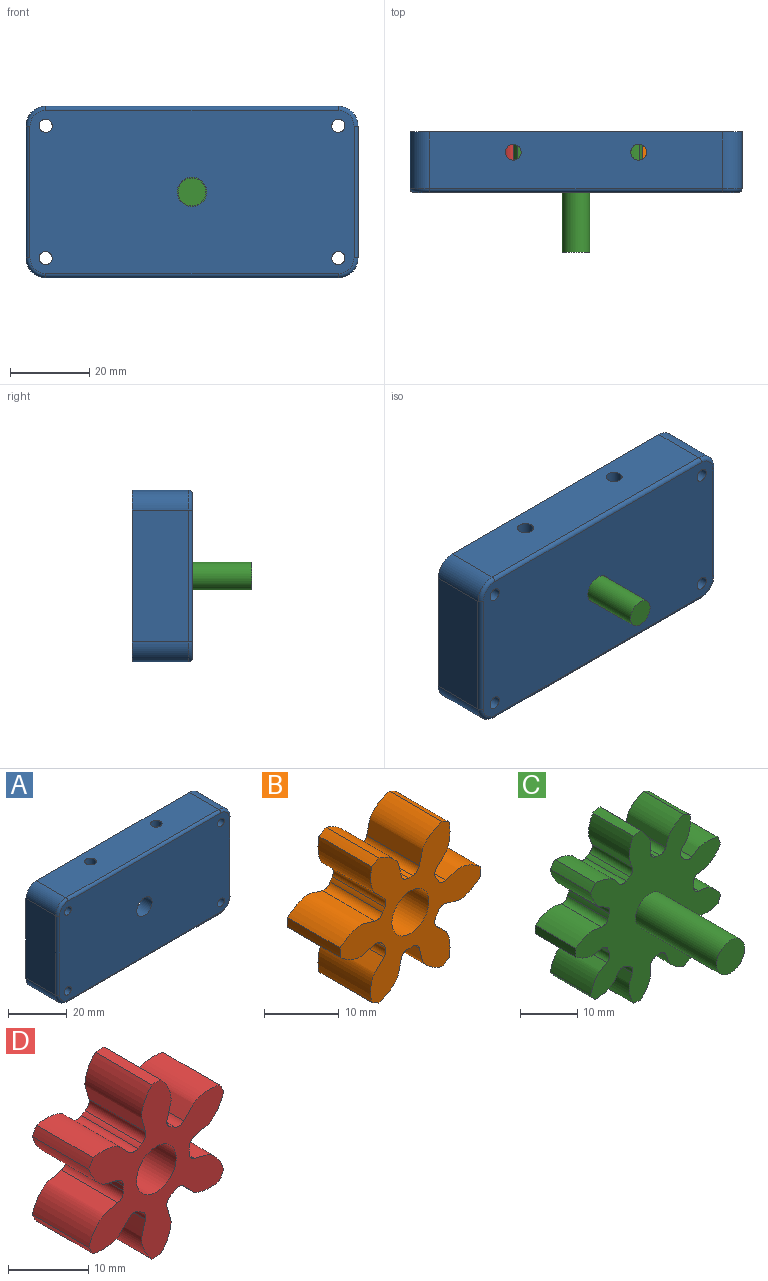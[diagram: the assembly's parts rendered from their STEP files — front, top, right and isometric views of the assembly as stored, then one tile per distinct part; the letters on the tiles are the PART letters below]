
ASSEMBLY  parts=4 mates=3
PART A: 36 faces, bbox 84.4x15.2x44 mm
  f0: cylinder r=13.6mm len=27.2mm, axis (0,1,0), area 631.5mm2, adj f1,f7,f8,f9,f12,f14
  f1: cylinder r=18.6mm len=31.59mm, axis (0,1,0), area 363.6mm2, adj f0,f2,f8,f9,f14,f15
  f2: cylinder r=13.6mm len=27.2mm, axis (0,1,0), area 631.5mm2, adj f1,f7,f8,f9,f13,f15
  f3: plane 33.2x14.2mm, normal (1,0,0), area 471.4mm2, adj f8,f20,f23,f27
  f4: plane 73.6x14.2mm, normal (0,0,1), area 1020mm2, adj f8,f14,f15,f20,f21,f24
  f5: plane 33.2x14.2mm, normal (-1,0,0), area 471.4mm2, adj f8,f21,f22,f28
  f6: plane 73.6x14.2mm, normal (0,0,-1), area 1020mm2, adj f8,f12,f13,f22,f23,f31
  f7: cylinder r=18.6mm len=31.59mm, axis (0,1,0), area 363.6mm2, adj f0,f2,f8,f9,f12,f13
  f8: plane 83.6x43.2mm, normal (0,1,0), area 1495.3mm2, adj f0,f1,f2,f3,f4,f5,f6,f7
  f9: plane 77.6x37.2mm, normal (0,1,0), area 1949.1mm2, adj f0,f1,f2,f7,f11,f32,f34
  f10: plane 81.6x41.2mm, normal (0,-1,0), area 3271mm2, adj f11,f16,f17,f18,f19,f24,f25,f26
  f11: cylinder r=3.7mm len=7.4mm, axis (0,-1,0), area 116.2mm2, adj f9,f10
  f12: cylinder r=2mm len=11.78mm, axis (0,0,1), area 130.4mm2, adj f0,f6,f7
  f13: cylinder r=2mm len=11.78mm, axis (0,0,1), area 130.4mm2, adj f2,f6,f7
  f14: cylinder r=2mm len=11.78mm, axis (0,0,1), area 130.4mm2, adj f0,f1,f4
  f15: cylinder r=2mm len=11.78mm, axis (0,0,1), area 130.4mm2, adj f1,f2,f4
  f16: cylinder r=1.65mm len=15.2mm, axis (0,1,0), area 157.6mm2, adj f8,f10
  f17: cylinder r=1.65mm len=15.2mm, axis (0,1,0), area 157.6mm2, adj f8,f10
  f18: cylinder r=1.65mm len=15.2mm, axis (0,1,0), area 157.6mm2, adj f8,f10
  f19: cylinder r=1.65mm len=15.2mm, axis (0,1,0), area 157.6mm2, adj f8,f10
  f20: cylinder r=5mm len=14.2mm, axis (0,-1,0), area 111.5mm2, adj f3,f4,f8,f25
  f21: cylinder r=5mm len=14.2mm, axis (0,1,0), area 111.5mm2, adj f4,f5,f8,f26
  f22: cylinder r=5mm len=14.2mm, axis (0,-1,0), area 111.5mm2, adj f5,f6,f8,f30
  f23: cylinder r=5mm len=14.2mm, axis (0,1,0), area 111.5mm2, adj f3,f6,f8,f29
  f24: cylinder r=1mm len=73.6mm, axis (1,0,0), area 115.6mm2, adj f4,f10,f25,f26
  f25: torus R=4mm, axis (0,-1,0), area 11.4mm2, adj f10,f20,f24,f27
  f26: torus R=4mm, axis (0,-1,0), area 11.4mm2, adj f10,f21,f24,f28
  f27: cylinder r=1mm len=33.2mm, axis (0,0,-1), area 52.2mm2, adj f3,f10,f25,f29
  f28: cylinder r=1mm len=33.2mm, axis (0,0,1), area 52.2mm2, adj f5,f10,f26,f30
  f29: torus R=4mm, axis (0,-1,0), area 11.4mm2, adj f10,f23,f27,f31
  f30: torus R=4mm, axis (0,-1,0), area 11.4mm2, adj f10,f22,f28,f31
  f31: cylinder r=1mm len=73.6mm, axis (-1,0,0), area 115.6mm2, adj f6,f10,f29,f30
  f32: cylinder r=3.3mm len=10.2mm, axis (0,-1,0), area 211.5mm2, adj f9,f33
  f33: plane 6.6x6.6mm, normal (0,1,0), area 34.2mm2, adj f32
  f34: cylinder r=3.3mm len=10.2mm, axis (0,-1,0), area 211.5mm2, adj f9,f35
  f35: plane 6.6x6.6mm, normal (0,1,0), area 34.2mm2, adj f34
PART B: 39 faces, bbox 26.8x10x24 mm
  f0: cylinder r=13.33mm len=10mm, axis (0,1,0), area 15.7mm2, adj f5,f7,f23,f35
  f1: cylinder r=13.33mm len=10mm, axis (0,1,0), area 15.7mm2, adj f5,f7,f30,f33
  f2: cylinder r=13.33mm len=10mm, axis (0,1,0), area 15.7mm2, adj f5,f7,f18,f25
  f3: cylinder r=13.33mm len=10mm, axis (0,1,0), area 15.7mm2, adj f5,f7,f8,f20
  f4: cylinder r=13.33mm len=10mm, axis (0,1,0), area 15.7mm2, adj f5,f7,f15,f28
  f5: plane 26.81x24.03mm, normal (0,-1,0), area 257.9mm2, adj f0,f1,f2,f3,f4,f6,f8,f9
  f6: cylinder r=13.33mm len=10mm, axis (0,1,0), area 15.7mm2, adj f5,f7,f10,f13
  f7: plane 26.81x24.03mm, normal (0,1,0), area 257.9mm2, adj f0,f1,f2,f3,f4,f6,f8,f9
  f8: extruded ~10x6.28mm, area 71.4mm2, adj f3,f5,f7,f11
  f9: cylinder r=5.83mm len=10mm, axis (0,1,0), area 8mm2, adj f5,f7,f11,f12
  f10: extruded ~10x6.6mm, area 71.4mm2, adj f5,f6,f7,f12
  f11: cylinder r=1.26mm len=10mm, axis (0,1,0), area 17.5mm2, adj f5,f7,f8,f9
  f12: cylinder r=1.26mm len=10mm, axis (0,1,0), area 17.5mm2, adj f5,f7,f9,f10
  f13: extruded ~10x6.6mm, area 71.4mm2, adj f5,f6,f7,f16
  f14: cylinder r=5.83mm len=10mm, axis (0,1,0), area 8mm2, adj f5,f7,f16,f17
  f15: extruded ~10x6.28mm, area 71.4mm2, adj f4,f5,f7,f17
  f16: cylinder r=1.26mm len=10mm, axis (0,1,0), area 17.5mm2, adj f5,f7,f13,f14
  f17: cylinder r=1.26mm len=10mm, axis (0,1,0), area 17.5mm2, adj f5,f7,f14,f15
  f18: extruded ~10x5.15mm, area 71.4mm2, adj f2,f5,f7,f21
  f19: cylinder r=5.83mm len=10mm, axis (0,1,0), area 8mm2, adj f5,f7,f21,f22
  f20: extruded ~10x5.15mm, area 71.4mm2, adj f3,f5,f7,f22
  f21: cylinder r=1.26mm len=10mm, axis (0,1,0), area 17.5mm2, adj f5,f7,f18,f19
  f22: cylinder r=1.26mm len=10mm, axis (0,1,0), area 17.5mm2, adj f5,f7,f19,f20
  f23: extruded ~10x6.6mm, area 71.4mm2, adj f0,f5,f7,f26
  f24: cylinder r=5.83mm len=10mm, axis (0,1,0), area 8mm2, adj f5,f7,f26,f27
  f25: extruded ~10x6.28mm, area 71.4mm2, adj f2,f5,f7,f27
  f26: cylinder r=1.26mm len=10mm, axis (0,1,0), area 17.5mm2, adj f5,f7,f23,f24
  f27: cylinder r=1.26mm len=10mm, axis (0,1,0), area 17.5mm2, adj f5,f7,f24,f25
  f28: extruded ~10x5.15mm, area 71.4mm2, adj f4,f5,f7,f31
  f29: cylinder r=5.83mm len=10mm, axis (0,1,0), area 8mm2, adj f5,f7,f31,f32
  f30: extruded ~10x5.15mm, area 71.4mm2, adj f1,f5,f7,f32
  f31: cylinder r=1.26mm len=10mm, axis (0,1,0), area 17.5mm2, adj f5,f7,f28,f29
  f32: cylinder r=1.26mm len=10mm, axis (0,1,0), area 17.5mm2, adj f5,f7,f29,f30
  f33: extruded ~10x6.28mm, area 71.4mm2, adj f1,f5,f7,f36
  f34: cylinder r=5.83mm len=10mm, axis (0,1,0), area 8mm2, adj f5,f7,f36,f37
  f35: extruded ~10x6.6mm, area 71.4mm2, adj f0,f5,f7,f37
  f36: cylinder r=1.26mm len=10mm, axis (0,1,0), area 17.5mm2, adj f5,f7,f33,f34
  f37: cylinder r=1.26mm len=10mm, axis (0,1,0), area 17.5mm2, adj f5,f7,f34,f35
  f38: cylinder r=3.5mm len=10mm, axis (0,-1,0), area 219.9mm2, adj f5,f7
PART C: 58 faces, bbox 36x30x36.5 mm
  f0: cylinder r=18.33mm len=10mm, axis (0,1,0), area 18.9mm2, adj f8,f10,f36,f53
  f1: cylinder r=18.33mm len=10mm, axis (0,1,0), area 18.9mm2, adj f8,f10,f48,f51
  f2: cylinder r=18.33mm len=10mm, axis (0,1,0), area 18.9mm2, adj f8,f10,f26,f43
  f3: cylinder r=18.33mm len=10mm, axis (0,1,0), area 18.9mm2, adj f8,f10,f38,f41
  f4: cylinder r=18.33mm len=10mm, axis (0,1,0), area 18.9mm2, adj f8,f10,f16,f33
  f5: cylinder r=18.33mm len=10mm, axis (0,1,0), area 18.9mm2, adj f8,f10,f28,f31
  f6: cylinder r=18.33mm len=10mm, axis (0,1,0), area 18.9mm2, adj f8,f10,f11,f23
  f7: cylinder r=18.33mm len=10mm, axis (0,1,0), area 18.9mm2, adj f8,f10,f18,f21
  f8: plane 36.53x35.98mm, normal (0,-1,0), area 635mm2, adj f0,f1,f2,f3,f4,f5,f6,f7
  f9: cylinder r=18.33mm len=10mm, axis (0,1,0), area 18.9mm2, adj f8,f10,f13,f46
  f10: plane 36.53x35.98mm, normal (0,1,0), area 673.5mm2, adj f0,f1,f2,f3,f4,f5,f6,f7
  f11: extruded ~10x5.56mm, area 68.1mm2, adj f6,f8,f10,f14
  f12: cylinder r=10.83mm len=10mm, axis (0,1,0), area 10.3mm2, adj f8,f10,f14,f15
  f13: extruded ~10x5.56mm, area 68.1mm2, adj f8,f9,f10,f15
  f14: cylinder r=1.36mm len=10mm, axis (0,1,0), area 19.9mm2, adj f8,f10,f11,f12
  f15: cylinder r=1.36mm len=10mm, axis (0,1,0), area 19.9mm2, adj f8,f10,f12,f13
  f16: extruded ~10x6.07mm, area 68.1mm2, adj f4,f8,f10,f19
  f17: cylinder r=10.83mm len=10mm, axis (0,1,0), area 10.3mm2, adj f8,f10,f19,f20
  f18: extruded ~10x4.88mm, area 68.1mm2, adj f7,f8,f10,f20
  f19: cylinder r=1.36mm len=10mm, axis (0,1,0), area 19.9mm2, adj f8,f10,f16,f17
  f20: cylinder r=1.36mm len=10mm, axis (0,1,0), area 19.9mm2, adj f8,f10,f17,f18
  f21: extruded ~10x6.22mm, area 68.1mm2, adj f7,f8,f10,f24
  f22: cylinder r=10.83mm len=10mm, axis (0,1,0), area 10.3mm2, adj f8,f10,f24,f25
  f23: extruded ~10x6.48mm, area 68.1mm2, adj f6,f8,f10,f25
  f24: cylinder r=1.36mm len=10mm, axis (0,1,0), area 19.9mm2, adj f8,f10,f21,f22
  f25: cylinder r=1.36mm len=10mm, axis (0,1,0), area 19.9mm2, adj f8,f10,f22,f23
  f26: extruded ~10x6.41mm, area 68.1mm2, adj f2,f8,f10,f29
  f27: cylinder r=10.83mm len=10mm, axis (0,1,0), area 10.3mm2, adj f8,f10,f29,f30
  f28: extruded ~10x5.15mm, area 68.1mm2, adj f5,f8,f10,f30
  f29: cylinder r=1.36mm len=10mm, axis (0,1,0), area 19.9mm2, adj f8,f10,f26,f27
  f30: cylinder r=1.36mm len=10mm, axis (0,1,0), area 19.9mm2, adj f8,f10,f27,f28
  f31: extruded ~10x5.77mm, area 68.1mm2, adj f5,f8,f10,f34
  f32: cylinder r=10.83mm len=10mm, axis (0,1,0), area 10.3mm2, adj f8,f10,f34,f35
  f33: extruded ~10x6.54mm, area 68.1mm2, adj f4,f8,f10,f35
  f34: cylinder r=1.36mm len=10mm, axis (0,1,0), area 19.9mm2, adj f8,f10,f31,f32
  f35: cylinder r=1.36mm len=10mm, axis (0,1,0), area 19.9mm2, adj f8,f10,f32,f33
  f36: extruded ~10x6.54mm, area 68.1mm2, adj f0,f8,f10,f39
  f37: cylinder r=10.83mm len=10mm, axis (0,1,0), area 10.3mm2, adj f8,f10,f39,f40
  f38: extruded ~10x5.77mm, area 68.1mm2, adj f3,f8,f10,f40
  f39: cylinder r=1.36mm len=10mm, axis (0,1,0), area 19.9mm2, adj f8,f10,f36,f37
  f40: cylinder r=1.36mm len=10mm, axis (0,1,0), area 19.9mm2, adj f8,f10,f37,f38
  f41: extruded ~10x5.15mm, area 68.1mm2, adj f3,f8,f10,f44
  f42: cylinder r=10.83mm len=10mm, axis (0,1,0), area 10.3mm2, adj f8,f10,f44,f45
  f43: extruded ~10x6.41mm, area 68.1mm2, adj f2,f8,f10,f45
  f44: cylinder r=1.36mm len=10mm, axis (0,1,0), area 19.9mm2, adj f8,f10,f41,f42
  f45: cylinder r=1.36mm len=10mm, axis (0,1,0), area 19.9mm2, adj f8,f10,f42,f43
  f46: extruded ~10x6.48mm, area 68.1mm2, adj f8,f9,f10,f49
  f47: cylinder r=10.83mm len=10mm, axis (0,1,0), area 10.3mm2, adj f8,f10,f49,f50
  f48: extruded ~10x6.22mm, area 68.1mm2, adj f1,f8,f10,f50
  f49: cylinder r=1.36mm len=10mm, axis (0,1,0), area 19.9mm2, adj f8,f10,f46,f47
  f50: cylinder r=1.36mm len=10mm, axis (0,1,0), area 19.9mm2, adj f8,f10,f47,f48
  f51: extruded ~10x4.88mm, area 68.1mm2, adj f1,f8,f10,f54
  f52: cylinder r=10.83mm len=10mm, axis (0,1,0), area 10.3mm2, adj f8,f10,f54,f55
  f53: extruded ~10x6.07mm, area 68.1mm2, adj f0,f8,f10,f55
  f54: cylinder r=1.36mm len=10mm, axis (0,1,0), area 19.9mm2, adj f8,f10,f51,f52
  f55: cylinder r=1.36mm len=10mm, axis (0,1,0), area 19.9mm2, adj f8,f10,f52,f53
  f56: cylinder r=3.5mm len=20mm, axis (0,1,0), area 439.8mm2, adj f8,f57
  f57: plane 7x7mm, normal (0,-1,0), area 38.5mm2, adj f56
PART D: 39 faces, bbox 24x10x26.8 mm
  f0: cylinder r=13.33mm len=10mm, axis (0,1,0), area 15.7mm2, adj f5,f7,f23,f35
  f1: cylinder r=13.33mm len=10mm, axis (0,1,0), area 15.7mm2, adj f5,f7,f30,f33
  f2: cylinder r=13.33mm len=10mm, axis (0,1,0), area 15.7mm2, adj f5,f7,f18,f25
  f3: cylinder r=13.33mm len=10mm, axis (0,1,0), area 15.7mm2, adj f5,f7,f8,f20
  f4: cylinder r=13.33mm len=10mm, axis (0,1,0), area 15.7mm2, adj f5,f7,f15,f28
  f5: plane 26.81x24.03mm, normal (0,-1,0), area 257.9mm2, adj f0,f1,f2,f3,f4,f6,f8,f9
  f6: cylinder r=13.33mm len=10mm, axis (0,1,0), area 15.7mm2, adj f5,f7,f10,f13
  f7: plane 26.81x24.03mm, normal (0,1,0), area 257.9mm2, adj f0,f1,f2,f3,f4,f6,f8,f9
  f8: extruded ~10x5.15mm, area 71.4mm2, adj f3,f5,f7,f11
  f9: cylinder r=5.83mm len=10mm, axis (0,1,0), area 8mm2, adj f5,f7,f11,f12
  f10: extruded ~10x5.15mm, area 71.4mm2, adj f5,f6,f7,f12
  f11: cylinder r=1.26mm len=10mm, axis (0,1,0), area 17.5mm2, adj f5,f7,f8,f9
  f12: cylinder r=1.26mm len=10mm, axis (0,1,0), area 17.5mm2, adj f5,f7,f9,f10
  f13: extruded ~10x6.28mm, area 71.4mm2, adj f5,f6,f7,f16
  f14: cylinder r=5.83mm len=10mm, axis (0,1,0), area 8mm2, adj f5,f7,f16,f17
  f15: extruded ~10x6.6mm, area 71.4mm2, adj f4,f5,f7,f17
  f16: cylinder r=1.26mm len=10mm, axis (0,1,0), area 17.5mm2, adj f5,f7,f13,f14
  f17: cylinder r=1.26mm len=10mm, axis (0,1,0), area 17.5mm2, adj f5,f7,f14,f15
  f18: extruded ~10x6.6mm, area 71.4mm2, adj f2,f5,f7,f21
  f19: cylinder r=5.83mm len=10mm, axis (0,1,0), area 8mm2, adj f5,f7,f21,f22
  f20: extruded ~10x6.28mm, area 71.4mm2, adj f3,f5,f7,f22
  f21: cylinder r=1.26mm len=10mm, axis (0,1,0), area 17.5mm2, adj f5,f7,f18,f19
  f22: cylinder r=1.26mm len=10mm, axis (0,1,0), area 17.5mm2, adj f5,f7,f19,f20
  f23: extruded ~10x6.28mm, area 71.4mm2, adj f0,f5,f7,f26
  f24: cylinder r=5.83mm len=10mm, axis (0,1,0), area 8mm2, adj f5,f7,f26,f27
  f25: extruded ~10x6.6mm, area 71.4mm2, adj f2,f5,f7,f27
  f26: cylinder r=1.26mm len=10mm, axis (0,1,0), area 17.5mm2, adj f5,f7,f23,f24
  f27: cylinder r=1.26mm len=10mm, axis (0,1,0), area 17.5mm2, adj f5,f7,f24,f25
  f28: extruded ~10x6.6mm, area 71.4mm2, adj f4,f5,f7,f31
  f29: cylinder r=5.83mm len=10mm, axis (0,1,0), area 8mm2, adj f5,f7,f31,f32
  f30: extruded ~10x6.28mm, area 71.4mm2, adj f1,f5,f7,f32
  f31: cylinder r=1.26mm len=10mm, axis (0,1,0), area 17.5mm2, adj f5,f7,f28,f29
  f32: cylinder r=1.26mm len=10mm, axis (0,1,0), area 17.5mm2, adj f5,f7,f29,f30
  f33: extruded ~10x5.15mm, area 71.4mm2, adj f1,f5,f7,f36
  f34: cylinder r=5.83mm len=10mm, axis (0,1,0), area 8mm2, adj f5,f7,f36,f37
  f35: extruded ~10x5.15mm, area 71.4mm2, adj f0,f5,f7,f37
  f36: cylinder r=1.26mm len=10mm, axis (0,1,0), area 17.5mm2, adj f5,f7,f33,f34
  f37: cylinder r=1.26mm len=10mm, axis (0,1,0), area 17.5mm2, adj f5,f7,f34,f35
  f38: cylinder r=3.5mm len=10mm, axis (0,-1,0), area 219.9mm2, adj f5,f7
PLACE A t=(-15.6,-1.22,0.28)mm fixed
PLACE B rot(axis=(0,-1,0),50.3deg) t=(-6.51,-1.42,-19.1)mm
PLACE C rot(axis=(0,1,0),153.5deg) t=(-15.6,-1.42,0.28)mm
PLACE D rot(axis=(0,-1,0),50.3deg) t=(-24.7,-1.42,19.66)mm
MATE revolute D.f0 <-> A.f34  axis (0,-1,0) through (-40.8,-11.42,0.28)mm
MATE revolute B.f0 <-> A.f2  axis (0,-1,0) through (9.6,-11.42,0.28)mm
MATE revolute C.f0 <-> A.f7  axis (0,-1,0) through (-15.6,-11.42,0.28)mm
